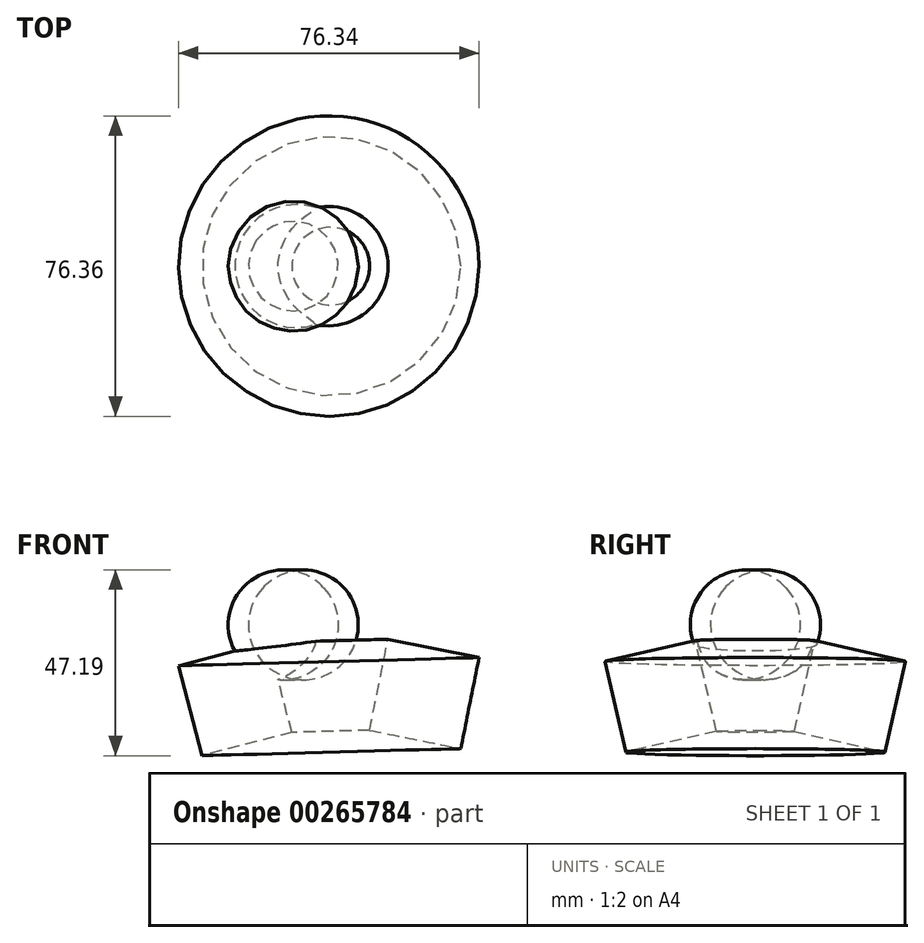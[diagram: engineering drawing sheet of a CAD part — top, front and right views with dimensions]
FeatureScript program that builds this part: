
annotation { "Feature Type Name" : "Feature", "Feature Type Description" : "" }
export const myFeature = defineFeature(function(context is Context, id is Id, definition is map)
    precondition{}
    {
        {
            var Q0;
            Q0=qCreatedBy(makeId("Front.planeOp"),FACE);
            var sketch = newSketch(context, id + "F0", { "sketchPlane" : qUnion([Q0])});
            skCircle(sketch, "E0.cCircle", {"center": v(-14.75, 4.06) * mm, "radius": 16.7 * mm, "construction": true});
            skLineSegment(sketch, "E0.0", {"start": v(-29.13, 12.54) * mm, "end": v(-6.27, 18.44) * mm});
            skLineSegment(sketch, "E0.1", {"start": v(-6.27, 18.44) * mm, "end": v(-0.37, -4.42) * mm});
            skLineSegment(sketch, "E0.2", {"start": v(-0.37, -4.42) * mm, "end": v(-23.23, -10.32) * mm});
            skLineSegment(sketch, "E0.3", {"start": v(-23.23, -10.32) * mm, "end": v(-29.13, 12.54) * mm});
            skSolve(sketch);
        }
        {
            var Q0;
            Q0=qCreatedBy(makeId("Front.planeOp"),FACE);
            var sketch = newSketch(context, id + "F1", { "sketchPlane" : qUnion([Q0])});
            skLineSegment(sketch, "E1", {"start": v(8.66, 27.47) * mm, "end": v(10.5, -40.56) * mm});
            skSolve(sketch);
        }
        {
            var Q0;
            Q0=makeQuery(id+"F0.imprint","IMPRINT",FACE,{"disambiguationData":[TD([[makeQuery(id+"F0.imprint","IMPRINT",EDGE,{"derivedFrom":sQuery(id+"F0.wireOp",EDGE,"E0.0")}),-1.0]])]});
            var Q1;
            Q1=sQuery(id+"F1.wireOp",EDGE,"E1");
            revolve(context, id + "F2", {"entities" : qUnion([Q0]), "axis" : qUnion([Q1]), "revolveType" : RevolveType.FULL});
        }
        {
            var Q0;
            Q0=qCreatedBy(makeId("Right.planeOp"),FACE);
            var sketch = newSketch(context, id + "F3", { "sketchPlane" : qUnion([Q0])});
            skArc(sketch, "E2", {"start": v(0, 9.2) * mm, "mid": v(16.52, 22.91) * mm, "end": v(0, 36.63) * mm});
            skLineSegment(sketch, "E3", {"start": v(0, 36.63) * mm, "end": v(0, 9.2) * mm});
            skSolve(sketch);
        }
        {
            var Q0;
            Q0=makeQuery(id+"F3.imprint","IMPRINT",FACE,{"disambiguationData":[TD([[makeQuery(id+"F3.imprint","IMPRINT",EDGE,{"derivedFrom":sQuery(id+"F3.wireOp",EDGE,"E2")}),1.0]])]});
            var Q1;
            Q1=sQuery(id+"F3.wireOp",EDGE,"E3");
            revolve(context, id + "F4", {"operationType" : NewBodyOperationType.ADD, "entities" : qUnion([Q0]), "axis" : qUnion([Q1]), "revolveType" : RevolveType.FULL});
        }
    });
